# Revit family: FP_Revit_18_OR90SCG6X1_Ranges_90001033A
name_source: partatom
category: Specialty Equipment
revit_build: Autodesk Revit 2018 (Build: 20170223_1515(x64)
units: mm (PartAtom-declared; Revit-internal decimal feet)

## family parameters
Always vertical = Yes
Cut with Voids When Loaded = Yes
OmniClass Number = 23.40.40.14.17.17
OmniClass Title = Ranges
Part Type = Normal
Room Calculation Point = No
Round Connector Dimension = Use Diameter
Shared = No
Work Plane-Based = No

## types (4) — shared parameters
Cavity - Depth = 600 mm  [stored 1.9685 ft]
Cavity - Height = 915 mm  [stored 3.00197 ft]
Cavity - Width = 900 mm  [stored 2.95276 ft]
Chassis - Depth = 600 mm  [stored 1.9685 ft]
Chassis - Height = 814 mm
Chassis - Width = 897 mm  [stored 2.94291 ft]
Clearance - Overhead Combustible = 650 mm  [stored 2.13255 ft]
Clearance - Overhead Non-Combustible = 450 mm  [stored 1.47638 ft]
Clearance - Overhead Rangehood = 650 mm  [stored 2.13255 ft]
Clearance - Side Combustible = 200 mm  [stored 0.656168 ft]
Connector Description - Electrical = 220-240 V, 50 Hz, 22.6 A
Connector Description - Gas = NG 1kPa, ULPG 2.75 kPa, Gas Connection to be Rp ½” (ISO 7-1) male
Countertop Height (min 898mm - max 946mm) = 915 mm  [stored 3.00197 ft]
Manufacturer = Fisher & Paykel Appliances
Material - Body = Fisher & Paykel - Stainless Steel
Material - Burners & Trivets = Fisher & Paykel - Black, Matte
Material - Buttons and Dials = Fisher & Paykel - Steel, Chrome Plated
Material - Door Front = Fisher & Paykel - Glass, Black
Material - Handle = Fisher & Paykel - Stainless Steel
Material - Trim = Fisher & Paykel - Steel, Chrome Plated
Product - Depth = 653 mm
Product - Height = 915 mm  [stored 3.00197 ft]
Product - Width = 897 mm  [stored 2.94291 ft]
URL = www.fisherpaykel.com
Visibility - Adjustable Feet Covers = Yes
Visibility - Clearance Required = Yes
Visibility - Rear Trim (Supplied) = Yes
Visibility - Toe Kick Panel (Optional) = Yes
zero-valued in all types: Clearance - Rear Combustible, Clearance - Rear Non-Combustible, Clearance - Side Non-Combustible

## per-type parameters (varying)
| type | Description | Material - COLOUR CHANGE | Model | Optional - Toe Kick Panel |
| OR90SCG6B (Black) | 90cm Classic Freestanding Dual Fuel Range (Black) | Fisher & Paykel - Black | OR390SCG6B1 | KICKOR90B1 |
| OR90SCG6W (White) | 90cm Classic Freestanding Dual Fuel Range (White) | Fisher & Paykel - White | OR90SCG6W1 | KICKOR90W1 |
| OR90SCG6R (Red) | 90cm Classic Freestanding Dual Fuel Range (Red) | Fisher & Paykel - Red | OR90SCG6R1 | KICKOR90R1 |
| OR90SCG6X (Stainless) | 90cm Classic Freestanding Dual Fuel Range (Stainless) | Fisher & Paykel - Stainless Steel | OR90SCG6X1 | KICKOR90X1 |

note: [stored X ft] marks values corroborated as IEEE doubles in the binary element streams (Revit-internal decimal feet)

## geometry (parser evidence)
native form markers: Sweep x24
no freeform markers — native parametric forms only
